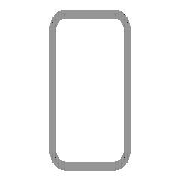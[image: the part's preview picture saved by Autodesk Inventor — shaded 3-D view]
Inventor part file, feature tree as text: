
AUTODESK INVENTOR PART (.ipt)
format: ipt  version: 2025 (Build 290162010, 162A)  size: 142,848 bytes
history: native  units: mm (DEFAULTED — no unit token found)
features: other x4, plane x2, split x1, sketch x1
ambient origin geometry x8: Origin, YZ Plane, XZ Plane, XY Plane, X Axis, Y Axis, Z Axis, Center Point
bodies: Solid1 (feature_tree), Body (feature_tree)
feature tree (8):
  parser-record x1  (decoder bookkeeping rows leaked as tree rows — omitted from the tree; the rows remain in map.json)
  other  "Driven Length"
  other  "Start Plane"
  other  "End Plane"
  plane  "Work Plane4"
  split  "Split1"
  sketch  "Sketch3"  dims[d3=608.634757mm d4=0.0mm d7=4.0mm d9=20.0mm d11=40.0mm d12=2.0mm d13=-0.0mm d14=608.634757mm d15=10.0mm d16=20.0mm d17=90.0deg d18=608.634757mm]
  plane  "Work Plane3"
